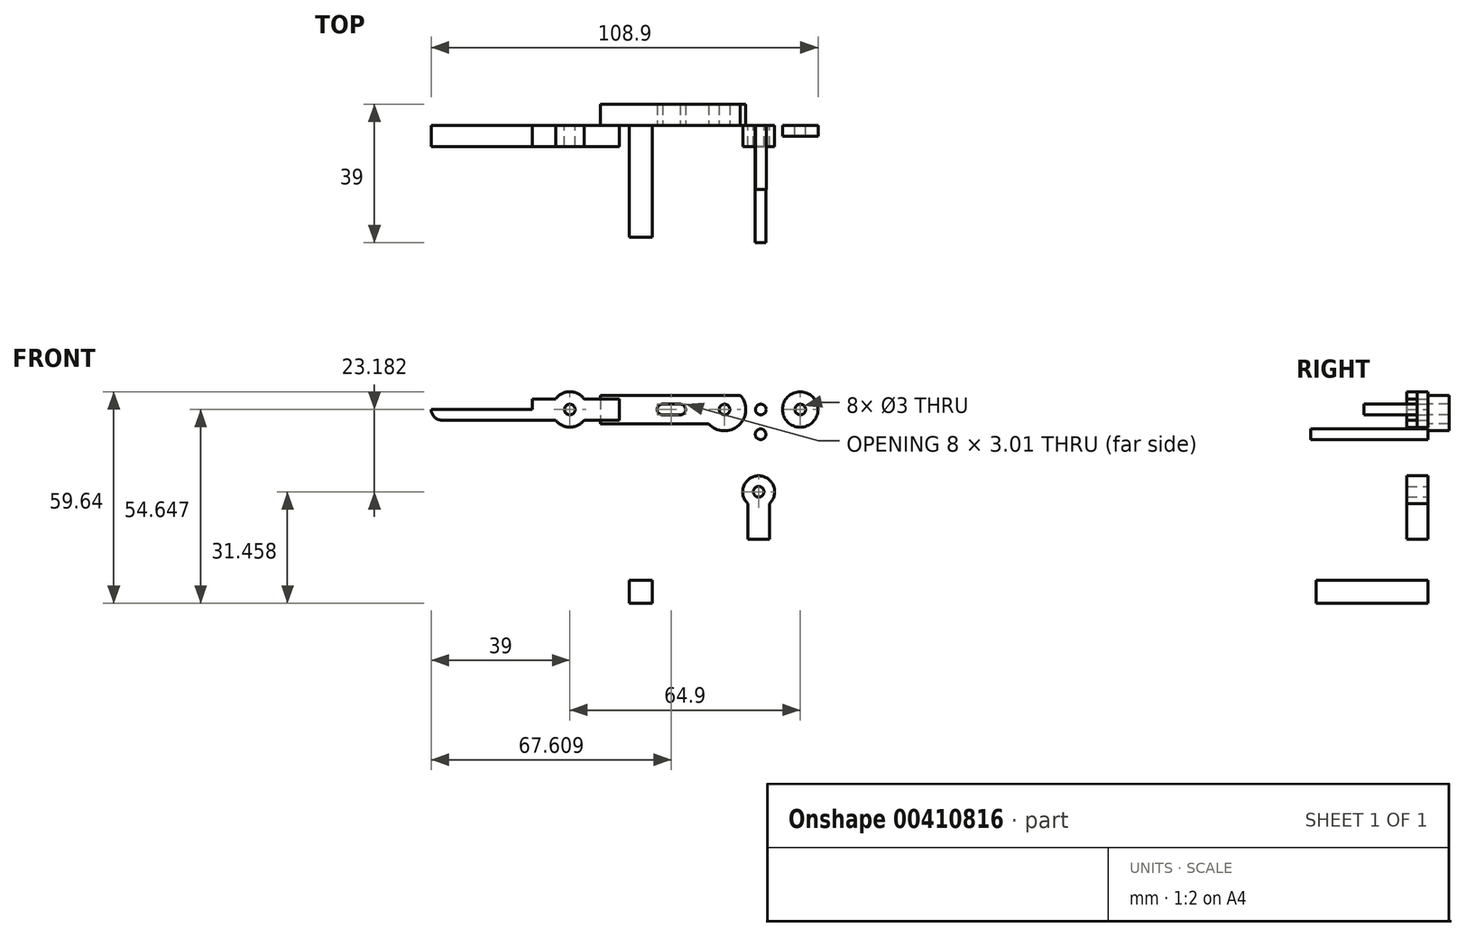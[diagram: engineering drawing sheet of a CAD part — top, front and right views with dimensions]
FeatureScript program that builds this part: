
annotation { "Feature Type Name" : "Feature", "Feature Type Description" : "" }
export const myFeature = defineFeature(function(context is Context, id is Id, definition is map)
    precondition{}
    {
        {
            var Q0;
            Q0=qCreatedBy(makeId("Front.planeOp"),FACE);
            var sketch = newSketch(context, id + "F0", { "sketchPlane" : qUnion([Q0])});
            skCircle(sketch, "E0", {"center": v(0, 0) * mm, "radius": 5 * mm});
            skCircle(sketch, "E1", {"center": v(0, 0) * mm, "radius": 1.5 * mm});
            skLineSegment(sketch, "E2.bottom", {"start": v(14, -3) * mm, "end": v(4, -3) * mm});
            skLineSegment(sketch, "E2.top", {"start": v(14, 3) * mm, "end": v(4, 3) * mm});
            skLineSegment(sketch, "E2.left", {"start": v(14, -3) * mm, "end": v(14, 3) * mm});
            skLineSegment(sketch, "E2.right", {"start": v(4, -3) * mm, "end": v(4, 3) * mm});
            skPoint(sketch, "E2.middle", {"position": v(4.24, 0) * mm});
            skLineSegment(sketch, "E3.bottom", {"start": v(-4, -3) * mm, "end": v(-36, -3) * mm});
            skLineSegment(sketch, "E3.top", {"start": v(-4, 3) * mm, "end": v(-10.55, 3) * mm});
            skLineSegment(sketch, "E3.left", {"start": v(-4, -3) * mm, "end": v(-4, 3) * mm});
            skLineSegment(sketch, "E3.right", {"start": v(-39, 0) * mm, "end": v(-39, 0) * mm});
            skPoint(sketch, "E3.middle", {"position": v(-10.56, 0) * mm});
            skLineSegment(sketch, "E4.top", {"start": v(-10.55, 0) * mm, "end": v(-39, 0) * mm});
            skLineSegment(sketch, "E4.left", {"start": v(-10.55, 3) * mm, "end": v(-10.55, 0) * mm});
            skPoint(sketch, "E5.visualSharp", {"position": v(-39, -3) * mm});
            skArc(sketch, "E5.filletArc", {"start": v(-39, 0) * mm, "mid": v(-38.12, -2.12) * mm, "end": v(-36, -3) * mm});
            skSolve(sketch);
        }
        {
            var Q0;
            Q0 = qSketchRegion(id + "F0", true);
            extrude(context, id + "F1", {"entities" : qUnion([Q0]), "depth" : 6 * mm});
        }
        {
            var Q0;
            Q0=makeQuery(id+"F1.opExtrude","CAP_FACE",FACE,{"disambiguationData":[OSD([sQuery(id+"F0.wireOp",EDGE,"E0"),sQuery(id+"F0.wireOp",EDGE,"E1"),sQuery(id+"F0.wireOp",EDGE,"E2.bottom"),sQuery(id+"F0.wireOp",EDGE,"E2.top"),sQuery(id+"F0.wireOp",EDGE,"E2.left"),sQuery(id+"F0.wireOp",EDGE,"E3.bottom"),sQuery(id+"F0.wireOp",EDGE,"E3.top"),sQuery(id+"F0.wireOp",EDGE,"E4.top"),sQuery(id+"F0.wireOp",EDGE,"E4.left"),sQuery(id+"F0.wireOp",EDGE,"E5.filletArc")])],"isStart":true});
            var sketch = newSketch(context, id + "F2", { "sketchPlane" : qUnion([Q0])});
            skLineSegment(sketch, "E6.bottom", {"start": v(-49.59, 4) * mm, "end": v(-8.59, 4) * mm});
            skLineSegment(sketch, "E6.top", {"start": v(-14.59, -4) * mm, "end": v(-8.59, -4) * mm});
            skLineSegment(sketch, "E6.right", {"start": v(-8.59, 3) * mm, "end": v(-8.59, -3) * mm});
            skLineSegment(sketch, "E7.top", {"start": v(-14.59, -4) * mm, "end": v(-49.59, -4) * mm});
            skLineSegment(sketch, "E7.right", {"start": v(-49.59, 3) * mm, "end": v(-49.59, -3) * mm});
            skCircle(sketch, "E8", {"center": v(-26.1, 0) * mm, "radius": 1.5 * mm});
            skCircle(sketch, "E9", {"center": v(-31.11, 0) * mm, "radius": 1.5 * mm});
            skLineSegment(sketch, "E10.bottom", {"start": v(-26.11, -1.5) * mm, "end": v(-31.11, -1.5) * mm});
            skLineSegment(sketch, "E10.top", {"start": v(-26.11, 1.51) * mm, "end": v(-31.11, 1.51) * mm});
            skLineSegment(sketch, "E10.left", {"start": v(-26.11, -1.5) * mm, "end": v(-26.11, 1.51) * mm});
            skLineSegment(sketch, "E10.right", {"start": v(-31.11, -1.5) * mm, "end": v(-31.11, 1.51) * mm});
            skCircle(sketch, "E11", {"center": v(-43.58, 0) * mm, "radius": 6 * mm});
            skCircle(sketch, "E12", {"center": v(-43.58, 0) * mm, "radius": 1.5 * mm});
            skLineSegment(sketch, "E13", {"start": v(-8.59, 4) * mm, "end": v(-8.59, 3) * mm});
            skLineSegment(sketch, "E14", {"start": v(-8.59, -4) * mm, "end": v(-8.59, -3) * mm});
            skLineSegment(sketch, "E15", {"start": v(-49.59, 3) * mm, "end": v(-49.59, 4) * mm});
            skLineSegment(sketch, "E16", {"start": v(-49.59, -3) * mm, "end": v(-49.59, -4) * mm});
            skSolve(sketch);
        }
        {
            var Q0;
            {var subQ0=sQuery(id+"F2.wireOp",EDGE,"E11");var subQ1=sQuery(id+"F2.wireOp",EDGE,"E6.bottom");var subQ2=makeQuery(id+"F2.imprint","INTERSECT",VERTEX,{"disambiguationData":[OD(0.0)],"derivedFrom":[subQ1,subQ0]});Q0=makeQuery(id+"F2.imprint","IMPRINT",FACE,{"disambiguationData":[TD([[makeQuery(id+"F2.imprint","IMPRINT",EDGE,{"disambiguationData":[TD([[subQ2,-1.0]])],"derivedFrom":subQ1}),1.0]])]});}
            var Q1;
            {var subQ0=sQuery(id+"F2.wireOp",EDGE,"E11");var subQ1=sQuery(id+"F2.wireOp",EDGE,"E7.top");var subQ2=makeQuery(id+"F2.imprint","INTERSECT",VERTEX,{"disambiguationData":[OD(0.0)],"derivedFrom":[subQ1,subQ0]});Q1=makeQuery(id+"F2.imprint","IMPRINT",FACE,{"disambiguationData":[TD([[makeQuery(id+"F2.imprint","IMPRINT",EDGE,{"disambiguationData":[TD([[subQ2,-1.0]])],"derivedFrom":subQ1}),1.0]])]});}
            var Q2;
            Q2=makeQuery(id+"F2.imprint","IMPRINT",FACE,{"disambiguationData":[TD([[makeQuery(id+"F2.imprint","IMPRINT",EDGE,{"derivedFrom":sQuery(id+"F2.wireOp",EDGE,"E12")}),-1.0]])]});
            var Q3;
            {var subQ0=sQuery(id+"F2.wireOp",EDGE,"E6.right");Q3=makeQuery(id+"F2.imprint","IMPRINT",FACE,{"disambiguationData":[TD([[makeQuery(id+"F2.imprint","IMPRINT",EDGE,{"derivedFrom":subQ0}),-1.0]])]});}
            var Q4;
            {var subQ12=sQuery(id+"F2.wireOp",EDGE,"E6.top");Q4=makeQuery(id+"F2.imprint","IMPRINT",FACE,{"disambiguationData":[TD([[makeQuery(id+"F2.imprint","IMPRINT",EDGE,{"derivedFrom":subQ12}),1.0]])]});}
            extrude(context, id + "F3", {"entities" : qUnion([Q0, Q1, Q2, Q3, Q4]), "operationType" : NewBodyOperationType.ADD, "depth" : 6 * mm});
        }
        {
            var Q0;
            Q0=qCreatedBy(makeId("Front.planeOp"),FACE);
            var sketch = newSketch(context, id + "F4", { "sketchPlane" : qUnion([Q0])});
            skCircle(sketch, "E17", {"center": v(64.9, 0) * mm, "radius": 5 * mm});
            skCircle(sketch, "E18", {"center": v(64.9, 0) * mm, "radius": 1.5 * mm});
            skSolve(sketch);
        }
        {
            var Q0;
            Q0 = qSketchRegion(id + "F4", true);
            extrude(context, id + "F5", {"entities" : qUnion([Q0]), "depth" : 3 * mm});
        }
        {
            var Q0;
            Q0=qCreatedBy(makeId("Front.planeOp"),FACE);
            var sketch = newSketch(context, id + "F6", { "sketchPlane" : qUnion([Q0])});
            skCircle(sketch, "E19", {"center": v(53.8, 0) * mm, "radius": 1.5 * mm});
            skSolve(sketch);
        }
        {
            var Q0;
            Q0 = qSketchRegion(id + "F6", true);
            extrude(context, id + "F7", {"entities" : qUnion([Q0]), "depth" : 18 * mm});
        }
        {
            var Q0;
            Q0=qCreatedBy(makeId("Front.planeOp"),FACE);
            var sketch = newSketch(context, id + "F8", { "sketchPlane" : qUnion([Q0])});
            skCircle(sketch, "E20", {"center": v(53.73, -6.97) * mm, "radius": 1.5 * mm});
            skSolve(sketch);
        }
        {
            var Q0;
            Q0 = qSketchRegion(id + "F8", true);
            extrude(context, id + "F9", {"entities" : qUnion([Q0]), "depth" : 33 * mm});
        }
        {
            var Q0;
            Q0=qCreatedBy(makeId("Front.planeOp"),FACE);
            var sketch = newSketch(context, id + "F10", { "sketchPlane" : qUnion([Q0])});
            skCircle(sketch, "E21", {"center": v(53.19, -23.18) * mm, "radius": 1.5 * mm});
            skCircle(sketch, "E22", {"center": v(53.19, -23.18) * mm, "radius": 4.5 * mm});
            skLineSegment(sketch, "E23.bottom", {"start": v(56.19, -36.53) * mm, "end": v(50.19, -36.53) * mm});
            skLineSegment(sketch, "E23.top", {"start": v(56.19, -26.53) * mm, "end": v(50.19, -26.53) * mm});
            skLineSegment(sketch, "E23.left", {"start": v(56.19, -36.53) * mm, "end": v(56.19, -26.53) * mm});
            skLineSegment(sketch, "E23.right", {"start": v(50.19, -36.53) * mm, "end": v(50.19, -26.53) * mm});
            skLineSegment(sketch, "E24", {"start": v(50.19, -30.53) * mm, "end": v(56.19, -30.53) * mm});
            skSolve(sketch);
        }
        {
            var Q0;
            Q0 = qSketchRegion(id + "F10", true);
            extrude(context, id + "F11", {"entities" : qUnion([Q0]), "depth" : 6 * mm});
        }
        {
            var Q0;
            Q0 = qSketchRegion(id + "F10", true);
            extrude(context, id + "F12", {"entities" : qUnion([Q0]), "operationType" : NewBodyOperationType.ADD, "depth" : 6 * mm});
        }
        {
            var Q0;
            Q0=qCreatedBy(makeId("Front.planeOp"),FACE);
            var sketch = newSketch(context, id + "F13", { "sketchPlane" : qUnion([Q0])});
            skLineSegment(sketch, "E25.bottom", {"start": v(23.2, -54.64) * mm, "end": v(16.7, -54.64) * mm});
            skLineSegment(sketch, "E25.top", {"start": v(23.2, -48.14) * mm, "end": v(16.7, -48.14) * mm});
            skLineSegment(sketch, "E25.left", {"start": v(23.2, -54.64) * mm, "end": v(23.2, -48.14) * mm});
            skLineSegment(sketch, "E25.right", {"start": v(16.7, -54.64) * mm, "end": v(16.7, -48.14) * mm});
            skPoint(sketch, "E25.middle", {"position": v(19.95, -51.4) * mm});
            skSolve(sketch);
        }
        {
            var Q0;
            Q0 = qSketchRegion(id + "F13", true);
            extrude(context, id + "F14", {"entities" : qUnion([Q0]), "depth" : 31.5 * mm});
        }
    });
